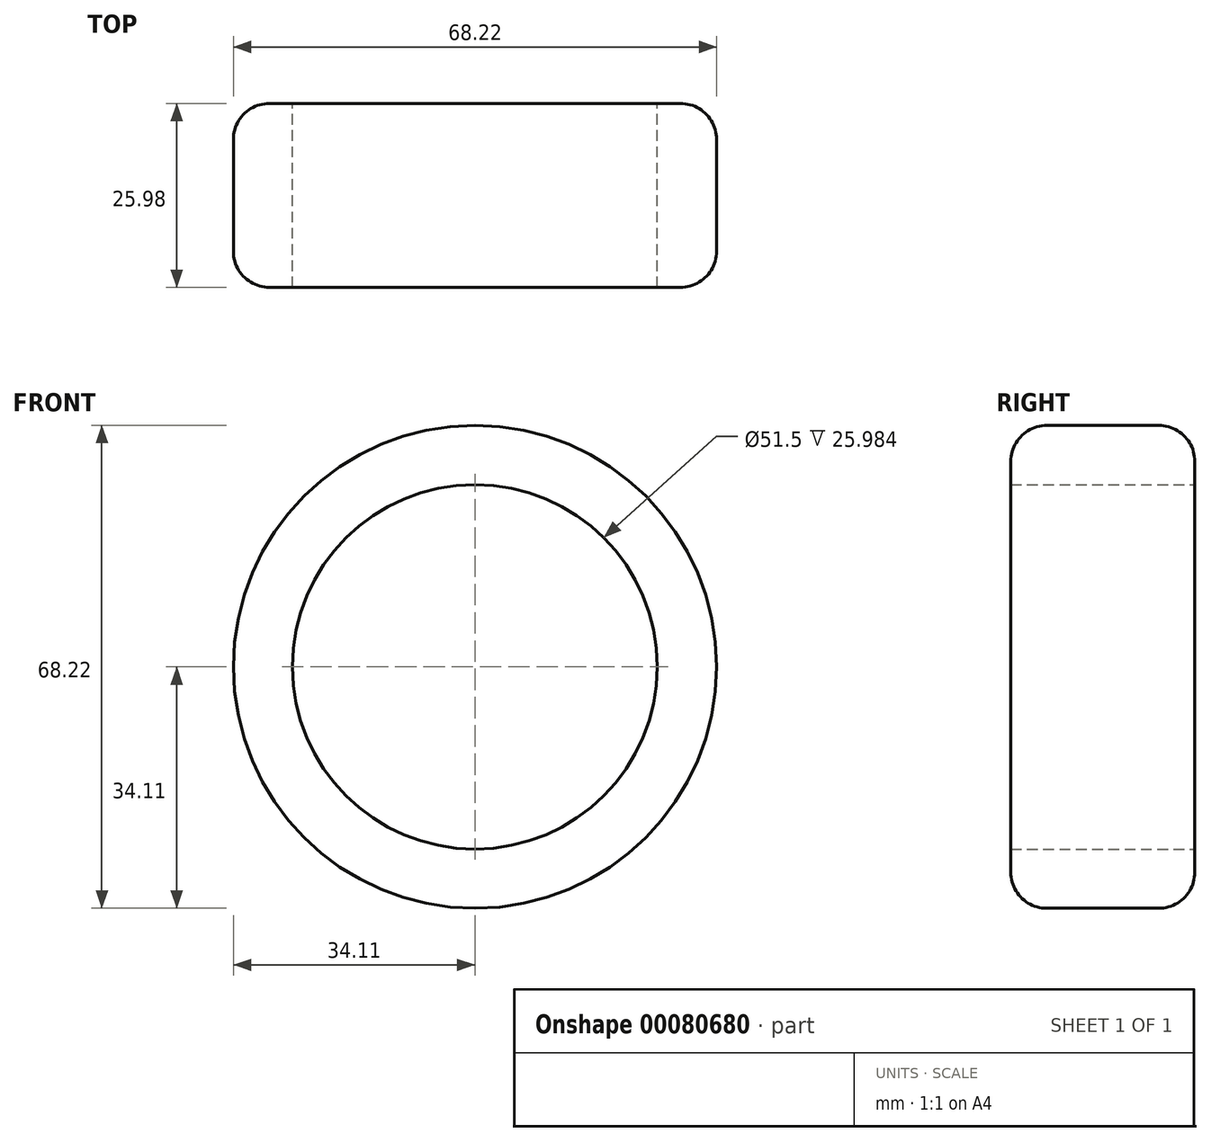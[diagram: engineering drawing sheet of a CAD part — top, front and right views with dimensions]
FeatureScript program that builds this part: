
annotation { "Feature Type Name" : "Feature", "Feature Type Description" : "" }
export const myFeature = defineFeature(function(context is Context, id is Id, definition is map)
    precondition{}
    {
        {
            var Q0;
            Q0=qCreatedBy(makeId("Front.planeOp"),FACE);
            var sketch = newSketch(context, id + "F0", { "sketchPlane" : qUnion([Q0])});
            skCircle(sketch, "E0", {"center": v(0, 0) * mm, "radius": 25.75 * mm});
            skCircle(sketch, "E1", {"center": v(0, 0) * mm, "radius": 34.1 * mm});
            skSolve(sketch);
        }
        {
            var Q0;
            Q0=makeQuery(id+"F0.imprint","IMPRINT",FACE,{"disambiguationData":[TD([[makeQuery(id+"F0.imprint","IMPRINT",EDGE,{"derivedFrom":sQuery(id+"F0.wireOp",EDGE,"E0")}),-1.0]])]});
            extrude(context, id + "F1", {"entities" : qUnion([Q0]), "depth" : 25.98 * mm});
        }
        {
            var Q0;
            Q0=makeQuery(id+"F1.opExtrude","SWEPT_FACE",FACE,{"disambiguationData":[OSD([sQuery(id+"F0.wireOp",EDGE,"E1")])]});
            fillet(context, id + "F2", {"entities" : qUnion([Q0]), "radius" : 5.08 * mm, "tangentPropagation" : true, "allowEdgeOverflow" : false});
        }
    });
